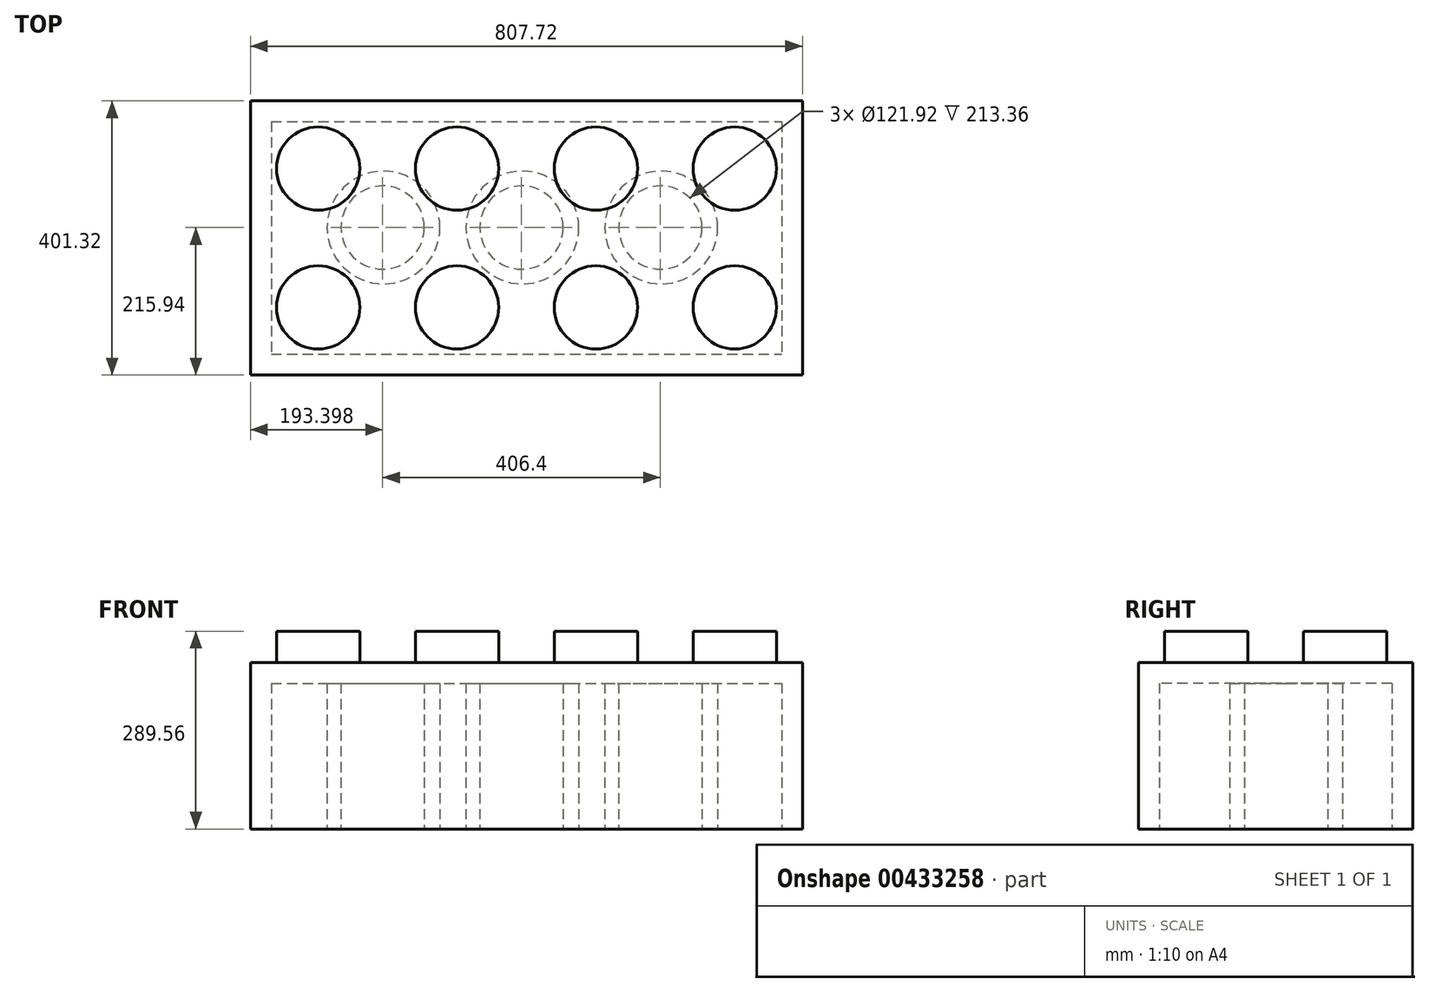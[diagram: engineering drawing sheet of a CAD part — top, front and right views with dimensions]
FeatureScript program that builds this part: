
annotation { "Feature Type Name" : "Feature", "Feature Type Description" : "" }
export const myFeature = defineFeature(function(context is Context, id is Id, definition is map)
    precondition{}
    {
        {
            var Q0;
            Q0=qCreatedBy(makeId("Top.planeOp"),FACE);
            var sketch = newSketch(context, id + "F0", { "sketchPlane" : qUnion([Q0])});
            skLineSegment(sketch, "E0.bottom", {"start": v(-434.65, 185.38) * mm, "end": v(373.07, 185.38) * mm});
            skLineSegment(sketch, "E0.top", {"start": v(-434.65, -215.94) * mm, "end": v(373.07, -215.94) * mm});
            skLineSegment(sketch, "E0.left", {"start": v(-434.65, 185.38) * mm, "end": v(-434.65, -215.94) * mm});
            skLineSegment(sketch, "E0.right", {"start": v(373.07, 185.38) * mm, "end": v(373.07, -215.94) * mm});
            skSolve(sketch);
        }
        {
            var Q0;
            Q0=qSketchRegion(id+"F0",true);
            extrude(context, id + "F1", {"entities" : qUnion([Q0]), "depth" : 243.84 * mm});
        }
        {
            var Q0;
            Q0=makeQuery(id+"F1.opExtrude","CAP_FACE",FACE,{"disambiguationData":[OSD([sQuery(id+"F0.wireOp",EDGE,"E0.bottom"),sQuery(id+"F0.wireOp",EDGE,"E0.top"),sQuery(id+"F0.wireOp",EDGE,"E0.left"),sQuery(id+"F0.wireOp",EDGE,"E0.right")])],"isStart":false});
            var sketch = newSketch(context, id + "F2", { "sketchPlane" : qUnion([Q0])});
            skCircle(sketch, "E1", {"center": v(-335.59, 86.32) * mm, "radius": 60.96 * mm});
            skCircle(sketch, "E2.0.1.0", {"center": v(-335.59, -116.88) * mm, "radius": 60.96 * mm});
            skCircle(sketch, "E2.1.0.0", {"center": v(-132.39, 86.32) * mm, "radius": 60.96 * mm});
            skCircle(sketch, "E2.1.1.0", {"center": v(-132.39, -116.88) * mm, "radius": 60.96 * mm});
            skCircle(sketch, "E2.2.0.0", {"center": v(70.81, 86.32) * mm, "radius": 60.96 * mm});
            skCircle(sketch, "E2.2.1.0", {"center": v(70.81, -116.88) * mm, "radius": 60.96 * mm});
            skCircle(sketch, "E2.3.0.0", {"center": v(274.01, 86.32) * mm, "radius": 60.96 * mm});
            skCircle(sketch, "E2.3.1.0", {"center": v(274.01, -116.88) * mm, "radius": 60.96 * mm});
            skLineSegment(sketch, "E2.direction1", {"start": v(-335.59, 86.32) * mm, "end": v(-132.39, 86.32) * mm, "construction": true});
            skLineSegment(sketch, "E2.direction2", {"start": v(-335.59, 86.32) * mm, "end": v(-335.59, -116.88) * mm, "construction": true});
            skSolve(sketch);
        }
        {
            var Q0;
            Q0=makeQuery(id+"F2.imprint","IMPRINT",FACE,{"disambiguationData":[TD([[makeQuery(id+"F2.imprint","IMPRINT",EDGE,{"derivedFrom":sQuery(id+"F2.wireOp",EDGE,"E2.0.1.0")}),1.0]])]});
            var Q1;
            Q1=makeQuery(id+"F2.imprint","IMPRINT",FACE,{"disambiguationData":[TD([[makeQuery(id+"F2.imprint","IMPRINT",EDGE,{"derivedFrom":sQuery(id+"F2.wireOp",EDGE,"E2.1.0.0")}),1.0]])]});
            var Q2;
            Q2=makeQuery(id+"F2.imprint","IMPRINT",FACE,{"disambiguationData":[TD([[makeQuery(id+"F2.imprint","IMPRINT",EDGE,{"derivedFrom":sQuery(id+"F2.wireOp",EDGE,"E2.1.1.0")}),1.0]])]});
            var Q3;
            Q3=makeQuery(id+"F2.imprint","IMPRINT",FACE,{"disambiguationData":[TD([[makeQuery(id+"F2.imprint","IMPRINT",EDGE,{"derivedFrom":sQuery(id+"F2.wireOp",EDGE,"E2.2.0.0")}),1.0]])]});
            var Q4;
            Q4=makeQuery(id+"F2.imprint","IMPRINT",FACE,{"disambiguationData":[TD([[makeQuery(id+"F2.imprint","IMPRINT",EDGE,{"derivedFrom":sQuery(id+"F2.wireOp",EDGE,"E2.3.1.0")}),1.0]])]});
            var Q5;
            Q5=makeQuery(id+"F2.imprint","IMPRINT",FACE,{"disambiguationData":[TD([[makeQuery(id+"F2.imprint","IMPRINT",EDGE,{"derivedFrom":sQuery(id+"F2.wireOp",EDGE,"E2.2.1.0")}),1.0]])]});
            var Q6;
            Q6=makeQuery(id+"F2.imprint","IMPRINT",FACE,{"disambiguationData":[TD([[makeQuery(id+"F2.imprint","IMPRINT",EDGE,{"derivedFrom":sQuery(id+"F2.wireOp",EDGE,"E2.3.0.0")}),1.0]])]});
            var Q7;
            Q7=makeQuery(id+"F2.imprint","IMPRINT",FACE,{"disambiguationData":[TD([[makeQuery(id+"F2.imprint","IMPRINT",EDGE,{"derivedFrom":sQuery(id+"F2.wireOp",EDGE,"E1")}),1.0]])]});
            extrude(context, id + "F3", {"entities" : qUnion([Q0, Q1, Q2, Q3, Q4, Q5, Q6, Q7]), "operationType" : NewBodyOperationType.ADD, "depth" : 45.72 * mm});
        }
        {
            var Q0;
            Q0=makeQuery(id+"F1.opExtrude","CAP_FACE",FACE,{"disambiguationData":[OSD([sQuery(id+"F0.wireOp",EDGE,"E0.bottom"),sQuery(id+"F0.wireOp",EDGE,"E0.top"),sQuery(id+"F0.wireOp",EDGE,"E0.left"),sQuery(id+"F0.wireOp",EDGE,"E0.right")])],"isStart":true});
            var sketch = newSketch(context, id + "F4", { "sketchPlane" : qUnion([Q0])});
            skCircle(sketch, "E3", {"center": v(166.4, 0) * mm, "radius": 82.55 * mm});
            skCircle(sketch, "E4.1.0.0", {"center": v(-36.8, 0) * mm, "radius": 82.55 * mm});
            skCircle(sketch, "E4.2.0.0", {"center": v(-240, 0) * mm, "radius": 82.55 * mm});
            skLineSegment(sketch, "E4.direction1", {"start": v(166.4, 0) * mm, "end": v(-36.8, 0) * mm, "construction": true});
            skSolve(sketch);
        }
        {
            var Q0;
            Q0=makeQuery(id+"F4.imprint","IMPRINT",FACE,{"disambiguationData":[TD([[makeQuery(id+"F4.imprint","IMPRINT",EDGE,{"derivedFrom":sQuery(id+"F4.wireOp",EDGE,"E3")}),-1.0]])]});
            var sketch = newSketch(context, id + "F5", { "sketchPlane" : qUnion([Q0])});
            skCircle(sketch, "E5", {"center": v(165.15, 0) * mm, "radius": 60.96 * mm});
            skCircle(sketch, "E6.1.0.0", {"center": v(-38.05, 0) * mm, "radius": 60.96 * mm});
            skCircle(sketch, "E6.2.0.0", {"center": v(-241.25, 0) * mm, "radius": 60.96 * mm});
            skLineSegment(sketch, "E6.direction1", {"start": v(165.15, 0) * mm, "end": v(-38.05, 0) * mm, "construction": true});
            skSolve(sketch);
        }
        {
            var Q0;
            Q0=makeQuery(id+"F4.imprint","IMPRINT",FACE,{"disambiguationData":[TD([[makeQuery(id+"F4.imprint","IMPRINT",EDGE,{"derivedFrom":sQuery(id+"F4.wireOp",EDGE,"E3")}),-1.0]])]});
            var sketch = newSketch(context, id + "F6", { "sketchPlane" : qUnion([Q0])});
            skLineSegment(sketch, "E7.bottom", {"start": v(-404.17, -154.9) * mm, "end": v(342.6, -154.9) * mm});
            skLineSegment(sketch, "E7.top", {"start": v(-404.17, 185.46) * mm, "end": v(342.6, 185.46) * mm});
            skLineSegment(sketch, "E7.left", {"start": v(-404.17, -154.9) * mm, "end": v(-404.17, 185.46) * mm});
            skLineSegment(sketch, "E7.right", {"start": v(342.6, -154.9) * mm, "end": v(342.6, 185.46) * mm});
            skSolve(sketch);
        }
        {
            var Q0;
            Q0=makeQuery(id+"F6.imprint","IMPRINT",FACE,{"disambiguationData":[TD([[makeQuery(id+"F6.imprint","IMPRINT",EDGE,{"derivedFrom":sQuery(id+"F6.wireOp",EDGE,"E7.bottom")}),1.0]])]});
            extrude(context, id + "F7", {"entities" : qUnion([Q0]), "operationType" : NewBodyOperationType.REMOVE, "oppositeDirection" : true, "depth" : 213.36 * mm});
        }
        {
            var Q0;
            Q0=qSketchRegion(id+"F5",true);
            extrude(context, id + "F8", {"entities" : qUnion([Q0]), "operationType" : NewBodyOperationType.REMOVE, "oppositeDirection" : true, "depth" : 213.36 * mm});
        }
    });
